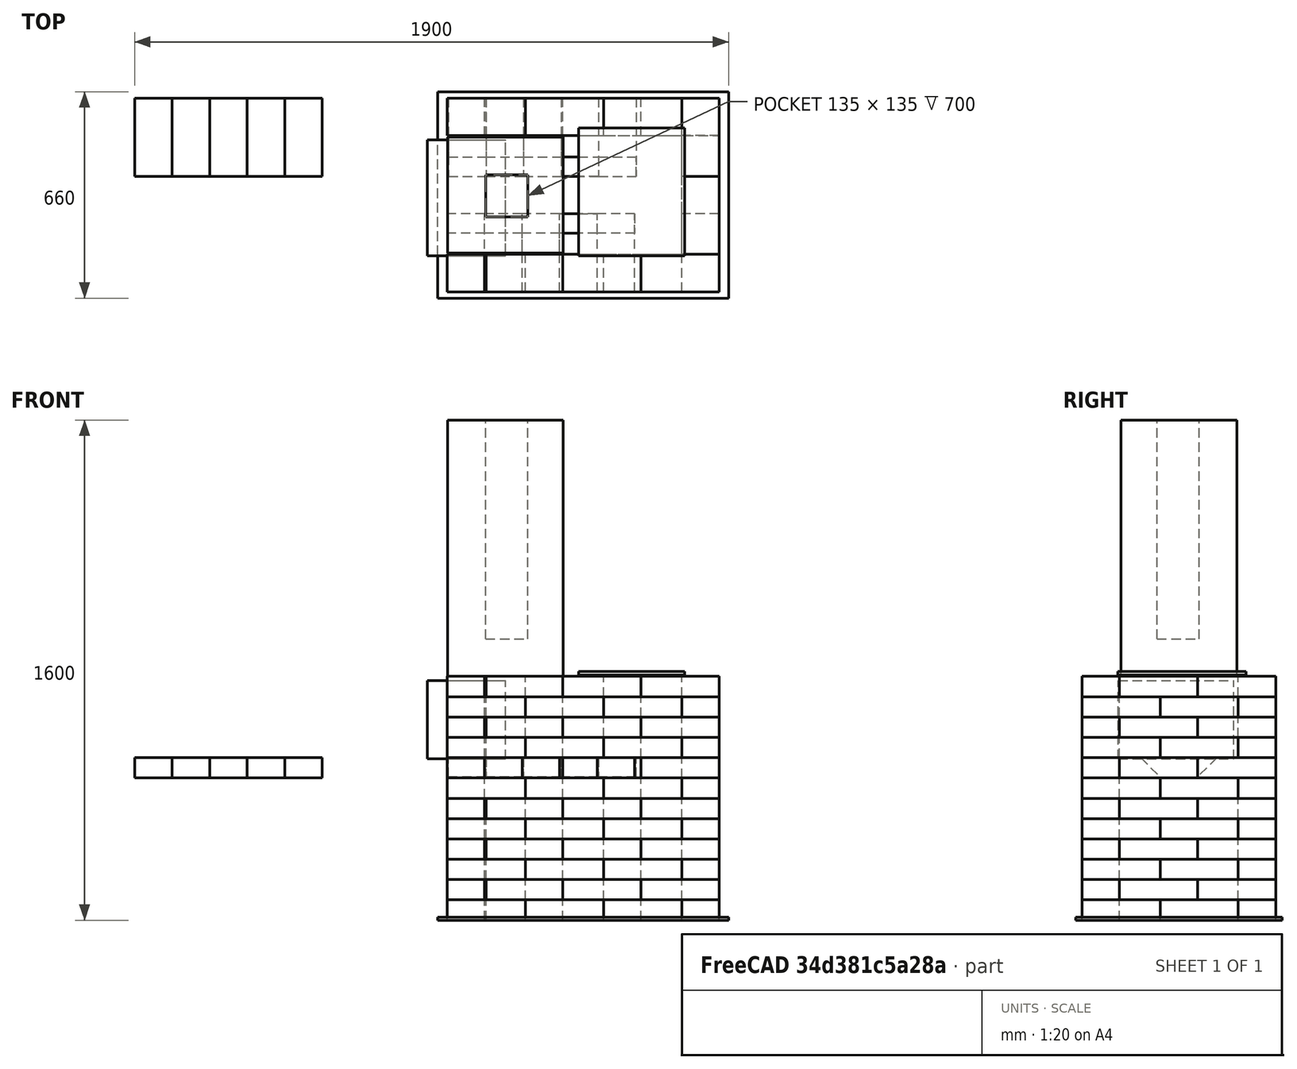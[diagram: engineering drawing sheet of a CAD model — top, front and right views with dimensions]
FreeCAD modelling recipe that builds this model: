
FCSTD DOCUMENT  (FreeCAD 0.19R24291 (Git))
Label: печьАрйка
License: All rights reserved
LicenseURL: http://en.wikipedia.org/wiki/All_rights_reserved
objects: Part::Box×136, Part::Compound×41, Part::Cut×3
note: 180 computed .brp shape members not serialized (recipe doc carries the construction recipe); baked Part::Feature solids carry a one-line shape summary decoded from their .brp

FEATURE [Part::Box] Box  label="Кирпич"
  AttacherType = Attacher::AttachEngine3D
  Height = 65
  Length = 250
  Width = 120
FEATURE [Part::Box] Box001  label="Кирпич001"
  AttacherType = Attacher::AttachEngine3D
  Height = 65
  Length = 250
  Placement = pos=(250,0,0) rot=(0,0,1;0rad)
  Width = 120
FEATURE [Part::Box] Box002  label="Кирпич002"
  AttacherType = Attacher::AttachEngine3D
  Height = 65
  Length = 250
  Placement = pos=(500,0,0) rot=(0,0,1;0rad)
  Width = 120
FEATURE [Part::Compound] Compound
  Links = -> [Box,Box001,Box002]
FEATURE [Part::Box] Box003  label="Кирпич003"
  AttacherType = Attacher::AttachEngine3D
  Height = 65
  Length = 250
  Width = 120
FEATURE [Part::Box] Box004  label="Кирпич004"
  AttacherType = Attacher::AttachEngine3D
  Height = 65
  Length = 250
  Placement = pos=(250,0,0) rot=(0,0,1;0rad)
  Width = 120
FEATURE [Part::Box] Box005  label="Кирпич005"
  AttacherType = Attacher::AttachEngine3D
  Height = 65
  Length = 250
  Placement = pos=(500,0,0) rot=(0,0,1;0rad)
  Width = 120
FEATURE [Part::Compound] Compound001
  Links = -> [Box003,Box004,Box005]
  Placement = pos=(120,500,0) rot=(0,0,1;0rad)
FEATURE [Part::Box] Box008  label="Куб002"
  AttacherType = Attacher::AttachEngine3D
  Height = 65
  Length = 250
  Placement = pos=(870,250,0) rot=(0,0,1;1.5708rad)
  Width = 120
FEATURE [Part::Box] Box009  label="Куб003"
  AttacherType = Attacher::AttachEngine3D
  Height = 65
  Length = 250
  Placement = pos=(870,0,0) rot=(0,0,1;1.5708rad)
  Width = 120
FEATURE [Part::Box] Box010  label="Кирпич006"
  AttacherType = Attacher::AttachEngine3D
  Height = 65
  Length = 250
  Width = 120
FEATURE [Part::Box] Box011  label="Кирпич007"
  AttacherType = Attacher::AttachEngine3D
  Height = 65
  Length = 250
  Placement = pos=(250,0,0) rot=(0,0,1;0rad)
  Width = 120
FEATURE [Part::Box] Box012  label="Кирпич008"
  AttacherType = Attacher::AttachEngine3D
  Height = 65
  Length = 250
  Placement = pos=(500,0,0) rot=(0,0,1;0rad)
  Width = 120
FEATURE [Part::Compound] Compound003
  Links = -> [Box010,Box011,Box012]
  Placement = pos=(120,500,130) rot=(0,0,1;0rad)
FEATURE [Part::Compound] Compound004
  Links = -> [Box009,Box008]
FEATURE [Part::Box] Box013  label="Куб004"
  AttacherType = Attacher::AttachEngine3D
  Height = 65
  Length = 250
  Placement = pos=(870,250,0) rot=(0,0,1;1.5708rad)
  Width = 120
FEATURE [Part::Box] Box014  label="Куб005"
  AttacherType = Attacher::AttachEngine3D
  Height = 65
  Length = 250
  Placement = pos=(870,0,0) rot=(0,0,1;1.5708rad)
  Width = 120
FEATURE [Part::Compound] Compound005
  Links = -> [Box014,Box013]
  Placement = pos=(0,120,65) rot=(0,0,1;0rad)
FEATURE [Part::Box] Box015  label="Кирпич009"
  AttacherType = Attacher::AttachEngine3D
  Height = 65
  Length = 250
  Placement = pos=(250,0,0) rot=(0,0,1;0rad)
  Width = 120
FEATURE [Part::Box] Box016  label="Кирпич010"
  AttacherType = Attacher::AttachEngine3D
  Height = 65
  Length = 250
  Placement = pos=(500,0,0) rot=(0,0,1;0rad)
  Width = 120
FEATURE [Part::Box] Box017  label="Кирпич011"
  AttacherType = Attacher::AttachEngine3D
  Height = 65
  Length = 250
  Width = 120
FEATURE [Part::Compound] Compound006
  Links = -> [Box017,Box015,Box016]
  Placement = pos=(0,500,65) rot=(0,0,1;0rad)
FEATURE [Part::Box] Box018  label="Кирпич012"
  AttacherType = Attacher::AttachEngine3D
  Height = 65
  Length = 250
  Placement = pos=(250,0,0) rot=(0,0,1;0rad)
  Width = 120
FEATURE [Part::Box] Box019  label="Кирпич013"
  AttacherType = Attacher::AttachEngine3D
  Height = 65
  Length = 250
  Placement = pos=(500,0,0) rot=(0,0,1;0rad)
  Width = 120
FEATURE [Part::Box] Box020  label="Кирпич014"
  AttacherType = Attacher::AttachEngine3D
  Height = 65
  Length = 250
  Width = 120
FEATURE [Part::Compound] Compound007
  Links = -> [Box020,Box018,Box019]
  Placement = pos=(0,0,130) rot=(0,0,1;0rad)
FEATURE [Part::Box] Box021  label="Кирпич015"
  AttacherType = Attacher::AttachEngine3D
  Height = 65
  Length = 250
  Placement = pos=(250,0,0) rot=(0,0,1;0rad)
  Width = 120
FEATURE [Part::Box] Box022  label="Кирпич016"
  AttacherType = Attacher::AttachEngine3D
  Height = 65
  Length = 250
  Placement = pos=(500,0,0) rot=(0,0,1;0rad)
  Width = 120
FEATURE [Part::Box] Box023  label="Кирпич017"
  AttacherType = Attacher::AttachEngine3D
  Height = 65
  Length = 250
  Width = 120
FEATURE [Part::Compound] Compound008
  Links = -> [Box023,Box021,Box022]
  Placement = pos=(120,0,65) rot=(0,0,1;0rad)
FEATURE [Part::Box] Box024  label="Куб006"
  AttacherType = Attacher::AttachEngine3D
  Height = 65
  Length = 250
  Placement = pos=(870,250,0) rot=(0,0,1;1.5708rad)
  Width = 120
FEATURE [Part::Box] Box025  label="Куб007"
  AttacherType = Attacher::AttachEngine3D
  Height = 65
  Length = 250
  Placement = pos=(870,0,0) rot=(0,0,1;1.5708rad)
  Width = 120
FEATURE [Part::Compound] Compound009
  Links = -> [Box025,Box024]
  Placement = pos=(0,0,130) rot=(0,0,1;0rad)
FEATURE [Part::Box] Box026  label="Куб008"
  AttacherType = Attacher::AttachEngine3D
  Height = 65
  Length = 250
  Placement = pos=(870,250,0) rot=(0,0,1;1.5708rad)
  Width = 120
FEATURE [Part::Box] Box027  label="Куб009"
  AttacherType = Attacher::AttachEngine3D
  Height = 65
  Length = 250
  Placement = pos=(870,0,0) rot=(0,0,1;1.5708rad)
  Width = 120
FEATURE [Part::Compound] Compound010
  Links = -> [Box027,Box026]
  Placement = pos=(0,120,195) rot=(0,0,1;0rad)
FEATURE [Part::Box] Box028  label="Куб010"
  AttacherType = Attacher::AttachEngine3D
  Height = 65
  Length = 250
  Placement = pos=(870,250,0) rot=(0,0,1;1.5708rad)
  Width = 120
FEATURE [Part::Box] Box029  label="Куб011"
  AttacherType = Attacher::AttachEngine3D
  Height = 65
  Length = 250
  Placement = pos=(870,0,0) rot=(0,0,1;1.5708rad)
  Width = 120
FEATURE [Part::Compound] Compound011
  Links = -> [Box029,Box028]
  Placement = pos=(0,0,260) rot=(0,0,1;0rad)
FEATURE [Part::Box] Box030  label="Куб012"
  AttacherType = Attacher::AttachEngine3D
  Height = 65
  Length = 250
  Placement = pos=(870,250,0) rot=(0,0,1;1.5708rad)
  Width = 120
FEATURE [Part::Box] Box031  label="Куб013"
  AttacherType = Attacher::AttachEngine3D
  Height = 65
  Length = 250
  Placement = pos=(870,0,0) rot=(0,0,1;1.5708rad)
  Width = 120
FEATURE [Part::Compound] Compound012
  Links = -> [Box031,Box030]
  Placement = pos=(0,120,325) rot=(0,0,1;0rad)
FEATURE [Part::Box] Box032  label="Куб014"
  AttacherType = Attacher::AttachEngine3D
  Height = 65
  Length = 250
  Placement = pos=(870,250,0) rot=(0,0,1;1.5708rad)
  Width = 120
FEATURE [Part::Box] Box033  label="Куб015"
  AttacherType = Attacher::AttachEngine3D
  Height = 65
  Length = 250
  Placement = pos=(870,0,0) rot=(0,0,1;1.5708rad)
  Width = 120
FEATURE [Part::Compound] Compound013
  Links = -> [Box033,Box032]
  Placement = pos=(0,0,390) rot=(0,0,1;0rad)
FEATURE [Part::Box] Box034  label="Куб016"
  AttacherType = Attacher::AttachEngine3D
  Height = 65
  Length = 250
  Placement = pos=(870,250,0) rot=(0,0,1;1.5708rad)
  Width = 120
FEATURE [Part::Box] Box035  label="Куб017"
  AttacherType = Attacher::AttachEngine3D
  Height = 65
  Length = 250
  Placement = pos=(870,0,0) rot=(0,0,1;1.5708rad)
  Width = 120
FEATURE [Part::Compound] Compound014
  Links = -> [Box035,Box034]
  Placement = pos=(0,120,455) rot=(0,0,1;0rad)
FEATURE [Part::Box] Box036  label="Кирпич018"
  AttacherType = Attacher::AttachEngine3D
  Height = 65
  Length = 250
  Width = 120
FEATURE [Part::Box] Box037  label="Кирпич019"
  AttacherType = Attacher::AttachEngine3D
  Height = 65
  Length = 250
  Placement = pos=(250,0,0) rot=(0,0,1;0rad)
  Width = 120
FEATURE [Part::Box] Box038  label="Кирпич020"
  AttacherType = Attacher::AttachEngine3D
  Height = 65
  Length = 250
  Placement = pos=(500,0,0) rot=(0,0,1;0rad)
  Width = 120
FEATURE [Part::Compound] Compound015
  Links = -> [Box036,Box037,Box038]
  Placement = pos=(120,0,195) rot=(0,0,1;0rad)
FEATURE [Part::Box] Box039  label="Кирпич021"
  AttacherType = Attacher::AttachEngine3D
  Height = 65
  Length = 250
  Placement = pos=(250,0,0) rot=(0,0,1;0rad)
  Width = 120
FEATURE [Part::Box] Box040  label="Кирпич022"
  AttacherType = Attacher::AttachEngine3D
  Height = 65
  Length = 250
  Placement = pos=(500,0,0) rot=(0,0,1;0rad)
  Width = 120
FEATURE [Part::Box] Box041  label="Кирпич023"
  AttacherType = Attacher::AttachEngine3D
  Height = 65
  Length = 250
  Width = 120
FEATURE [Part::Compound] Compound016
  Links = -> [Box041,Box039,Box040]
  Placement = pos=(0,500,195) rot=(0,0,1;0rad)
FEATURE [Part::Box] Box042  label="Кирпич024"
  AttacherType = Attacher::AttachEngine3D
  Height = 65
  Length = 250
  Placement = pos=(250,0,0) rot=(0,0,1;0rad)
  Width = 120
FEATURE [Part::Box] Box043  label="Кирпич025"
  AttacherType = Attacher::AttachEngine3D
  Height = 65
  Length = 250
  Placement = pos=(500,0,0) rot=(0,0,1;0rad)
  Width = 120
FEATURE [Part::Box] Box044  label="Кирпич026"
  AttacherType = Attacher::AttachEngine3D
  Height = 65
  Length = 250
  Width = 120
FEATURE [Part::Compound] Compound017
  Links = -> [Box044,Box042,Box043]
  Placement = pos=(120,500,260) rot=(0,0,1;0rad)
FEATURE [Part::Box] Box045  label="Кирпич027"
  AttacherType = Attacher::AttachEngine3D
  Height = 65
  Length = 250
  Placement = pos=(250,0,0) rot=(0,0,1;0rad)
  Width = 120
FEATURE [Part::Box] Box046  label="Кирпич028"
  AttacherType = Attacher::AttachEngine3D
  Height = 65
  Length = 250
  Placement = pos=(500,0,0) rot=(0,0,1;0rad)
  Width = 120
FEATURE [Part::Box] Box047  label="Кирпич029"
  AttacherType = Attacher::AttachEngine3D
  Height = 65
  Length = 250
  Width = 120
FEATURE [Part::Compound] Compound018
  Links = -> [Box047,Box045,Box046]
  Placement = pos=(120,500,390) rot=(0,0,1;0rad)
FEATURE [Part::Box] Box048  label="Кирпич030"
  AttacherType = Attacher::AttachEngine3D
  Height = 65
  Length = 250
  Placement = pos=(250,0,0) rot=(0,0,1;0rad)
  Width = 120
FEATURE [Part::Box] Box049  label="Кирпич031"
  AttacherType = Attacher::AttachEngine3D
  Height = 65
  Length = 250
  Placement = pos=(500,0,0) rot=(0,0,1;0rad)
  Width = 120
FEATURE [Part::Box] Box050  label="Кирпич032"
  AttacherType = Attacher::AttachEngine3D
  Height = 65
  Length = 250
  Width = 120
FEATURE [Part::Compound] Compound019
  Links = -> [Box050,Box048,Box049]
  Placement = pos=(120,0,325) rot=(0,0,1;0rad)
FEATURE [Part::Box] Box051  label="Кирпич033"
  AttacherType = Attacher::AttachEngine3D
  Height = 65
  Length = 250
  Placement = pos=(500,0,0) rot=(0,0,1;0rad)
  Width = 120
FEATURE [Part::Box] Box052  label="Кирпич034"
  AttacherType = Attacher::AttachEngine3D
  Height = 65
  Length = 250
  Placement = pos=(250,0,0) rot=(0,0,1;0rad)
  Width = 120
FEATURE [Part::Box] Box053  label="Кирпич035"
  AttacherType = Attacher::AttachEngine3D
  Height = 65
  Length = 250
  Width = 120
FEATURE [Part::Compound] Compound020
  Links = -> [Box053,Box052,Box051]
  Placement = pos=(120,0,455) rot=(0,0,1;0rad)
FEATURE [Part::Box] Box054  label="Кирпич036"
  AttacherType = Attacher::AttachEngine3D
  Height = 65
  Length = 250
  Placement = pos=(500,0,0) rot=(0,0,1;0rad)
  Width = 120
FEATURE [Part::Box] Box055  label="Кирпич037"
  AttacherType = Attacher::AttachEngine3D
  Height = 65
  Length = 250
  Width = 120
FEATURE [Part::Box] Box056  label="Кирпич038"
  AttacherType = Attacher::AttachEngine3D
  Height = 65
  Length = 250
  Placement = pos=(250,0,0) rot=(0,0,1;0rad)
  Width = 120
FEATURE [Part::Compound] Compound021
  Links = -> [Box055,Box056,Box054]
  Placement = pos=(0,500,325) rot=(0,0,1;0rad)
FEATURE [Part::Box] Box057  label="Кирпич039"
  AttacherType = Attacher::AttachEngine3D
  Height = 65
  Length = 250
  Placement = pos=(500,0,0) rot=(0,0,1;0rad)
  Width = 120
FEATURE [Part::Box] Box058  label="Кирпич040"
  AttacherType = Attacher::AttachEngine3D
  Height = 65
  Length = 250
  Width = 120
FEATURE [Part::Box] Box059  label="Кирпич041"
  AttacherType = Attacher::AttachEngine3D
  Height = 65
  Length = 250
  Placement = pos=(250,0,0) rot=(0,0,1;0rad)
  Width = 120
FEATURE [Part::Box] Box060  label="Кирпич042"
  AttacherType = Attacher::AttachEngine3D
  Height = 65
  Length = 250
  Width = 120
FEATURE [Part::Box] Box061  label="Кирпич043"
  AttacherType = Attacher::AttachEngine3D
  Height = 65
  Length = 250
  Placement = pos=(250,0,0) rot=(0,0,1;0rad)
  Width = 120
FEATURE [Part::Box] Box062  label="Кирпич044"
  AttacherType = Attacher::AttachEngine3D
  Height = 65
  Length = 250
  Placement = pos=(500,0,0) rot=(0,0,1;0rad)
  Width = 120
FEATURE [Part::Compound] Compound023
  Links = -> [Box060,Box061,Box062]
  Placement = pos=(0,0,260) rot=(0,0,1;0rad)
FEATURE [Part::Box] Box063  label="Кирпич045"
  AttacherType = Attacher::AttachEngine3D
  Height = 65
  Length = 250
  Placement = pos=(250,0,0) rot=(0,0,1;0rad)
  Width = 120
FEATURE [Part::Box] Box064  label="Кирпич046"
  AttacherType = Attacher::AttachEngine3D
  Height = 65
  Length = 250
  Placement = pos=(500,0,0) rot=(0,0,1;0rad)
  Width = 120
FEATURE [Part::Box] Box065  label="Кирпич047"
  AttacherType = Attacher::AttachEngine3D
  Height = 65
  Length = 250
  Width = 120
FEATURE [Part::Compound] Compound024
  Links = -> [Box065,Box063,Box064]
  Placement = pos=(0,0,390) rot=(0,0,1;0rad)
FEATURE [Part::Box] Box066  label="Кирпич048"
  AttacherType = Attacher::AttachEngine3D
  Height = 65
  Length = 250
  Placement = pos=(250,0,0) rot=(0,0,1;0rad)
  Width = 120
FEATURE [Part::Box] Box067  label="Кирпич049"
  AttacherType = Attacher::AttachEngine3D
  Height = 65
  Length = 250
  Placement = pos=(500,0,0) rot=(0,0,1;0rad)
  Width = 120
FEATURE [Part::Box] Box068  label="Кирпич050"
  AttacherType = Attacher::AttachEngine3D
  Height = 65
  Length = 250
  Width = 120
FEATURE [Part::Compound] Compound025
  Links = -> [Box068,Box066,Box067]
  Placement = pos=(0,0,520) rot=(0,0,1;0rad)
FEATURE [Part::Box] Box069  label="Куб018"
  AttacherType = Attacher::AttachEngine3D
  Height = 65
  Length = 250
  Placement = pos=(870,0,0) rot=(0,0,1;1.5708rad)
  Width = 120
FEATURE [Part::Box] Box070  label="Куб019"
  AttacherType = Attacher::AttachEngine3D
  Height = 65
  Length = 250
  Placement = pos=(870,250,0) rot=(0,0,1;1.5708rad)
  Width = 120
FEATURE [Part::Compound] Compound026
  Links = -> [Box069,Box070]
  Placement = pos=(0,0,520) rot=(0,0,1;0rad)
FEATURE [Part::Box] Box071  label="Куб020"
  AttacherType = Attacher::AttachEngine3D
  Height = 65
  Length = 250
  Placement = pos=(870,250,0) rot=(0,0,1;1.5708rad)
  Width = 120
FEATURE [Part::Box] Box072  label="Куб021"
  AttacherType = Attacher::AttachEngine3D
  Height = 65
  Length = 250
  Placement = pos=(870,0,0) rot=(0,0,1;1.5708rad)
  Width = 120
FEATURE [Part::Compound] Compound027
  Links = -> [Box072,Box071]
  Placement = pos=(0,120,585) rot=(0,0,1;0rad)
FEATURE [Part::Box] Box073  label="Куб022"
  AttacherType = Attacher::AttachEngine3D
  Height = 65
  Length = 250
  Placement = pos=(870,250,0) rot=(0,0,1;1.5708rad)
  Width = 120
FEATURE [Part::Box] Box074  label="Куб023"
  AttacherType = Attacher::AttachEngine3D
  Height = 65
  Length = 250
  Placement = pos=(870,0,0) rot=(0,0,1;1.5708rad)
  Width = 120
FEATURE [Part::Box] Box075  label="Кирпич051"
  AttacherType = Attacher::AttachEngine3D
  Height = 65
  Length = 250
  Placement = pos=(250,0,0) rot=(0,0,1;0rad)
  Width = 120
FEATURE [Part::Box] Box076  label="Кирпич052"
  AttacherType = Attacher::AttachEngine3D
  Height = 65
  Length = 250
  Width = 120
FEATURE [Part::Box] Box077  label="Кирпич053"
  AttacherType = Attacher::AttachEngine3D
  Height = 65
  Length = 250
  Placement = pos=(500,0,0) rot=(0,0,1;0rad)
  Width = 120
FEATURE [Part::Compound] Compound029
  Links = -> [Box076,Box075,Box077]
  Placement = pos=(120,0,585) rot=(0,0,1;0rad)
FEATURE [Part::Box] Box078  label="Кирпич054"
  AttacherType = Attacher::AttachEngine3D
  Height = 65
  Length = 250
  Placement = pos=(250,0,0) rot=(0,0,1;0rad)
  Width = 120
FEATURE [Part::Box] Box079  label="Кирпич055"
  AttacherType = Attacher::AttachEngine3D
  Height = 65
  Length = 250
  Placement = pos=(500,0,0) rot=(0,0,1;0rad)
  Width = 120
FEATURE [Part::Box] Box080  label="Кирпич056"
  AttacherType = Attacher::AttachEngine3D
  Height = 65
  Length = 250
  Width = 120
FEATURE [Part::Compound] Compound030
  Links = -> [Box080,Box078,Box079]
  Placement = pos=(0,0,650) rot=(0,0,1;0rad)
FEATURE [Part::Box] Box081  label="Кирпич057"
  AttacherType = Attacher::AttachEngine3D
  Height = 65
  Length = 250
  Placement = pos=(250,0,0) rot=(0,0,1;0rad)
  Width = 120
FEATURE [Part::Box] Box082  label="Кирпич058"
  AttacherType = Attacher::AttachEngine3D
  Height = 65
  Length = 250
  Placement = pos=(500,0,0) rot=(0,0,1;0rad)
  Width = 120
FEATURE [Part::Box] Box083  label="Кирпич059"
  AttacherType = Attacher::AttachEngine3D
  Height = 65
  Length = 250
  Width = 120
FEATURE [Part::Compound] Compound031
  Links = -> [Box083,Box081,Box082]
  Placement = pos=(120,500,520) rot=(0,0,1;0rad)
FEATURE [Part::Box] Box084  label="Кирпич060"
  AttacherType = Attacher::AttachEngine3D
  Height = 65
  Length = 250
  Width = 120
FEATURE [Part::Box] Box085  label="Кирпич061"
  AttacherType = Attacher::AttachEngine3D
  Height = 65
  Length = 250
  Placement = pos=(500,0,0) rot=(0,0,1;0rad)
  Width = 120
FEATURE [Part::Box] Box086  label="Кирпич062"
  AttacherType = Attacher::AttachEngine3D
  Height = 65
  Length = 250
  Placement = pos=(250,0,0) rot=(0,0,1;0rad)
  Width = 120
FEATURE [Part::Compound] Compound032
  Links = -> [Box084,Box086,Box085]
  Placement = pos=(120,500,650) rot=(0,0,1;0rad)
FEATURE [Part::Box] Box087  label="Кирпич063"
  AttacherType = Attacher::AttachEngine3D
  Height = 65
  Length = 250
  Width = 120
FEATURE [Part::Box] Box088  label="Кирпич064"
  AttacherType = Attacher::AttachEngine3D
  Height = 65
  Length = 250
  Placement = pos=(500,0,0) rot=(0,0,1;0rad)
  Width = 120
FEATURE [Part::Box] Box089  label="Кирпич065"
  AttacherType = Attacher::AttachEngine3D
  Height = 65
  Length = 250
  Placement = pos=(250,0,0) rot=(0,0,1;0rad)
  Width = 120
FEATURE [Part::Compound] Compound033
  Links = -> [Box087,Box089,Box088]
  Placement = pos=(0,500,585) rot=(0,0,1;0rad)
FEATURE [Part::Compound] Compound028
  Links = -> [Box074,Box073]
  Placement = pos=(0,0,650) rot=(0,0,1;0rad)
FEATURE [Part::Box] Box090  label="Куб024"
  AttacherType = Attacher::AttachEngine3D
  Height = 65
  Length = 250
  Placement = pos=(120,0,455) rot=(0,0,1;1.5708rad)
  Width = 120
FEATURE [Part::Box] Box091  label="Кирпич066"
  AttacherType = Attacher::AttachEngine3D
  Height = 65
  Length = 250
  Placement = pos=(250,0,0) rot=(0,0,1;0rad)
  Width = 120
FEATURE [Part::Box] Box092  label="Кирпич067"
  AttacherType = Attacher::AttachEngine3D
  Height = 65
  Length = 250
  Placement = pos=(500,0,0) rot=(0,0,1;0rad)
  Width = 120
FEATURE [Part::Box] Box093  label="Кирпич068"
  AttacherType = Attacher::AttachEngine3D
  Height = 65
  Length = 250
  Width = 120
FEATURE [Part::Compound] Compound034
  Links = -> [Box093,Box091,Box092]
  Placement = pos=(120,0,715) rot=(0,0,1;0rad)
FEATURE [Part::Box] Box094  label="Кирпич069"
  AttacherType = Attacher::AttachEngine3D
  Height = 65
  Length = 250
  Placement = pos=(250,0,0) rot=(0,0,1;0rad)
  Width = 120
FEATURE [Part::Box] Box095  label="Кирпич070"
  AttacherType = Attacher::AttachEngine3D
  Height = 65
  Length = 250
  Placement = pos=(500,0,0) rot=(0,0,1;0rad)
  Width = 120
FEATURE [Part::Box] Box096  label="Кирпич071"
  AttacherType = Attacher::AttachEngine3D
  Height = 65
  Length = 250
  Width = 120
FEATURE [Part::Box] Box097  label="Куб025"
  AttacherType = Attacher::AttachEngine3D
  Height = 65
  Length = 250
  Placement = pos=(870,0,0) rot=(0,0,1;1.5708rad)
  Width = 120
FEATURE [Part::Box] Box098  label="Куб026"
  AttacherType = Attacher::AttachEngine3D
  Height = 65
  Length = 250
  Placement = pos=(870,250,0) rot=(0,0,1;1.5708rad)
  Width = 120
FEATURE [Part::Box] Box099  label="Куб027"
  AttacherType = Attacher::AttachEngine3D
  Height = 65
  Length = 250
  Placement = pos=(870,0,0) rot=(0,0,1;1.5708rad)
  Width = 120
FEATURE [Part::Box] Box100  label="Куб028"
  AttacherType = Attacher::AttachEngine3D
  Height = 65
  Length = 250
  Placement = pos=(870,250,0) rot=(0,0,1;1.5708rad)
  Width = 120
FEATURE [Part::Compound] Compound037
  Links = -> [Box099,Box100]
  Placement = pos=(0,120,715) rot=(0,0,1;0rad)
FEATURE [Part::Box] Box101  label="Плита"
  AttacherType = Attacher::AttachEngine3D
  Height = 11
  Length = 410
  Placement = pos=(760,115,785) rot=(0,0,1;1.5708rad)
  Width = 340
FEATURE [Part::Box] Box102  label="Основание"
  AttacherType = Attacher::AttachEngine3D
  Height = 10
  Length = 930
  Placement = pos=(-30,-20,0) rot=(0,0,1;0rad)
  Width = 660
FEATURE [Part::Box] Box103  label="Куб029"
  AttacherType = Attacher::AttachEngine3D
  Height = 65
  Length = 250
  Placement = pos=(240,0,455) rot=(0,0,1;1.5708rad)
  Width = 120
FEATURE [Part::Box] Box104  label="Куб030"
  AttacherType = Attacher::AttachEngine3D
  Height = 65
  Length = 250
  Placement = pos=(360,0,455) rot=(0,0,1;1.5708rad)
  Width = 120
FEATURE [Part::Box] Box105  label="Куб031"
  AttacherType = Attacher::AttachEngine3D
  Height = 65
  Length = 250
  Placement = pos=(480,0,455) rot=(0,0,1;1.5708rad)
  Width = 120
FEATURE [Part::Box] Box106  label="Куб032"
  AttacherType = Attacher::AttachEngine3D
  Height = 65
  Length = 250
  Placement = pos=(600,0,455) rot=(0,0,1;1.5708rad)
  Width = 120
FEATURE [Part::Compound] Compound038
  Links = -> [Box090,Box103,Box104,Box105,Box106]
  Placement = pos=(-1000,0,0) rot=(0,0,1;0rad)
FEATURE [Part::Box] Box107  label="Куб033"
  AttacherType = Attacher::AttachEngine3D
  Height = 65
  Length = 250
  Placement = pos=(240,0,455) rot=(0,0,1;1.5708rad)
  Width = 120
FEATURE [Part::Box] Box108  label="Куб034"
  AttacherType = Attacher::AttachEngine3D
  Height = 65
  Length = 250
  Placement = pos=(480,0,455) rot=(0,0,1;1.5708rad)
  Width = 120
FEATURE [Part::Box] Box109  label="Куб035"
  AttacherType = Attacher::AttachEngine3D
  Height = 65
  Length = 250
  Placement = pos=(600,0,455) rot=(0,0,1;1.5708rad)
  Width = 120
FEATURE [Part::Box] Box110  label="Куб036"
  AttacherType = Attacher::AttachEngine3D
  Height = 65
  Length = 250
  Placement = pos=(120,0,455) rot=(0,0,1;1.5708rad)
  Width = 120
FEATURE [Part::Box] Box111  label="Куб037"
  AttacherType = Attacher::AttachEngine3D
  Height = 65
  Length = 250
  Placement = pos=(360,0,455) rot=(0,0,1;1.5708rad)
  Width = 120
FEATURE [Part::Box] Box124  label="Кирпич074"
  AttacherType = Attacher::AttachEngine3D
  Height = 65
  Length = 250
  Placement = pos=(250,0,0) rot=(0,0,1;0rad)
  Width = 120
FEATURE [Part::Box] Box125  label="Кирпич075"
  AttacherType = Attacher::AttachEngine3D
  Height = 65
  Length = 250
  Placement = pos=(250,0,0) rot=(0,0,1;0rad)
  Width = 120
FEATURE [Part::Box] Box126  label="Кирпич076"
  AttacherType = Attacher::AttachEngine3D
  Height = 65
  Length = 250
  Width = 120
FEATURE [Part::Box] Box127  label="Кирпич077"
  AttacherType = Attacher::AttachEngine3D
  Height = 65
  Length = 250
  Placement = pos=(500,0,0) rot=(0,0,1;0rad)
  Width = 120
FEATURE [Part::Box] Box130  label="Куб"
  AttacherType = Attacher::AttachEngine3D
  Height = 250
  Length = 250
  Placement = pos=(-420,0,0) rot=(0,0,1;0rad)
  Width = 370
FEATURE [Part::Compound] Compound051  label="Камера"
  Links = -> [Box130]
  Placement = pos=(357,116,516) rot=(0,0,1;0rad)
FEATURE [Part::Box] Box131  label="Труба"
  AttacherType = Attacher::AttachEngine3D
  Height = 820
  Length = 370
  Placement = pos=(-1.79383,125,780) rot=(0,0,1;0rad)
  Width = 370
FEATURE [Part::Box] Box132  label="Труба001"
  AttacherType = Attacher::AttachEngine3D
  Height = 1000
  Length = 135
  Placement = pos=(120,240,900) rot=(0,0,1;0rad)
  Width = 135
FEATURE [Part::Cut] Cut
  Base = -> Box131
  Placement = pos=(3,0,0) rot=(0,0,1;0rad)
  Tool = -> Box132
FEATURE [Part::Box] Box133  label="Куб048"
  AttacherType = Attacher::AttachEngine3D
  Height = 120
  Length = 600
  Placement = pos=(-1000,251.73,456.377) rot=(1,0,0;0.785398rad)
  Width = 120
FEATURE [Part::Cut] Cut001
  Base = -> Compound038
  Placement = pos=(1000,0,0) rot=(0,0,1;0rad)
  Tool = -> Box133
FEATURE [Part::Box] Box134  label="Куб049"
  AttacherType = Attacher::AttachEngine3D
  Height = 65
  Length = 250
  Placement = pos=(120,0,455) rot=(0,0,1;1.5708rad)
  Width = 120
FEATURE [Part::Box] Box135  label="Куб050"
  AttacherType = Attacher::AttachEngine3D
  Height = 65
  Length = 250
  Placement = pos=(240,0,455) rot=(0,0,1;1.5708rad)
  Width = 120
FEATURE [Part::Box] Box136  label="Куб051"
  AttacherType = Attacher::AttachEngine3D
  Height = 65
  Length = 250
  Placement = pos=(360,0,455) rot=(0,0,1;1.5708rad)
  Width = 120
FEATURE [Part::Box] Box137  label="Куб052"
  AttacherType = Attacher::AttachEngine3D
  Height = 65
  Length = 250
  Placement = pos=(480,0,455) rot=(0,0,1;1.5708rad)
  Width = 120
FEATURE [Part::Box] Box138  label="Куб053"
  AttacherType = Attacher::AttachEngine3D
  Height = 65
  Length = 250
  Placement = pos=(600,0,455) rot=(0,0,1;1.5708rad)
  Width = 120
FEATURE [Part::Compound] Compound053
  Links = -> [Box134,Box135,Box136,Box137,Box138]
  Placement = pos=(-1000,0,0) rot=(0,0,1;0rad)
FEATURE [Part::Box] Box139  label="Куб054"
  AttacherType = Attacher::AttachEngine3D
  Height = 120
  Length = 600
  Placement = pos=(-1000,251.73,456.377) rot=(1,0,0;0.785398rad)
  Width = 120
FEATURE [Part::Cut] Cut002
  Base = -> Compound053
  Placement = pos=(-396,620,0) rot=(0,0,1;3.14159rad)
  Tool = -> Box139
FEATURE [Part::Compound] Compound039
  Links = -> [Box110,Box107,Box111,Box108,Box109]
  Placement = pos=(-1000,370,0) rot=(0,0,1;0rad)
FEATURE [Part::Box] Box140  label="Кирпич078"
  AttacherType = Attacher::AttachEngine3D
  Height = 65
  Length = 125
  Placement = pos=(0,0,65) rot=(0,0,1;0rad)
  Width = 120
FEATURE [Part::Box] Box141  label="Кирпич079"
  AttacherType = Attacher::AttachEngine3D
  Height = 65
  Length = 125
  Placement = pos=(0,0,195) rot=(0,0,1;0rad)
  Width = 120
FEATURE [Part::Box] Box142  label="Кирпич080"
  AttacherType = Attacher::AttachEngine3D
  Height = 65
  Length = 125
  Placement = pos=(0,0,325) rot=(0,0,1;0rad)
  Width = 120
FEATURE [Part::Box] Box143  label="Кирпич081"
  AttacherType = Attacher::AttachEngine3D
  Height = 65
  Length = 125
  Placement = pos=(0,0,715) rot=(0,0,1;0rad)
  Width = 120
FEATURE [Part::Box] Box144  label="Кирпич082"
  AttacherType = Attacher::AttachEngine3D
  Height = 65
  Length = 125
  Placement = pos=(0,0,585) rot=(0,0,1;0rad)
  Width = 120
FEATURE [Part::Compound] Compound054
  Links = -> [Box143,Box144,Box142,Box141,Box140]
FEATURE [Part::Box] Box145  label="Кирпич083"
  AttacherType = Attacher::AttachEngine3D
  Height = 65
  Length = 125
  Placement = pos=(0,0,195) rot=(0,0,1;0rad)
  Width = 120
FEATURE [Part::Box] Box146  label="Кирпич084"
  AttacherType = Attacher::AttachEngine3D
  Height = 65
  Length = 125
  Placement = pos=(0,0,325) rot=(0,0,1;0rad)
  Width = 120
FEATURE [Part::Box] Box147  label="Кирпич085"
  AttacherType = Attacher::AttachEngine3D
  Height = 65
  Length = 125
  Placement = pos=(0,0,585) rot=(0,0,1;0rad)
  Width = 120
FEATURE [Part::Box] Box148  label="Кирпич086"
  AttacherType = Attacher::AttachEngine3D
  Height = 65
  Length = 125
  Placement = pos=(0,0,715) rot=(0,0,1;0rad)
  Width = 120
FEATURE [Part::Box] Box149  label="Кирпич087"
  AttacherType = Attacher::AttachEngine3D
  Height = 65
  Length = 125
  Placement = pos=(0,0,65) rot=(0,0,1;0rad)
  Width = 120
FEATURE [Part::Compound] Compound055
  Links = -> [Box148,Box147,Box146,Box145,Box149]
  Placement = pos=(0,500,-65) rot=(0,0,1;0rad)
FEATURE [Part::Box] Box123  label="Кирпич073"
  AttacherType = Attacher::AttachEngine3D
  Height = 65
  Length = 250
  Placement = pos=(500,0,0) rot=(0,0,1;0rad)
  Width = 120
FEATURE [Part::Box] Box122  label="Кирпич072"
  AttacherType = Attacher::AttachEngine3D
  Height = 65
  Length = 250
  Width = 120
FEATURE [Part::Compound] Compound045
  Links = -> [Box122,Box124,Box123]
  Placement = pos=(0,500,715) rot=(0,0,1;0rad)
